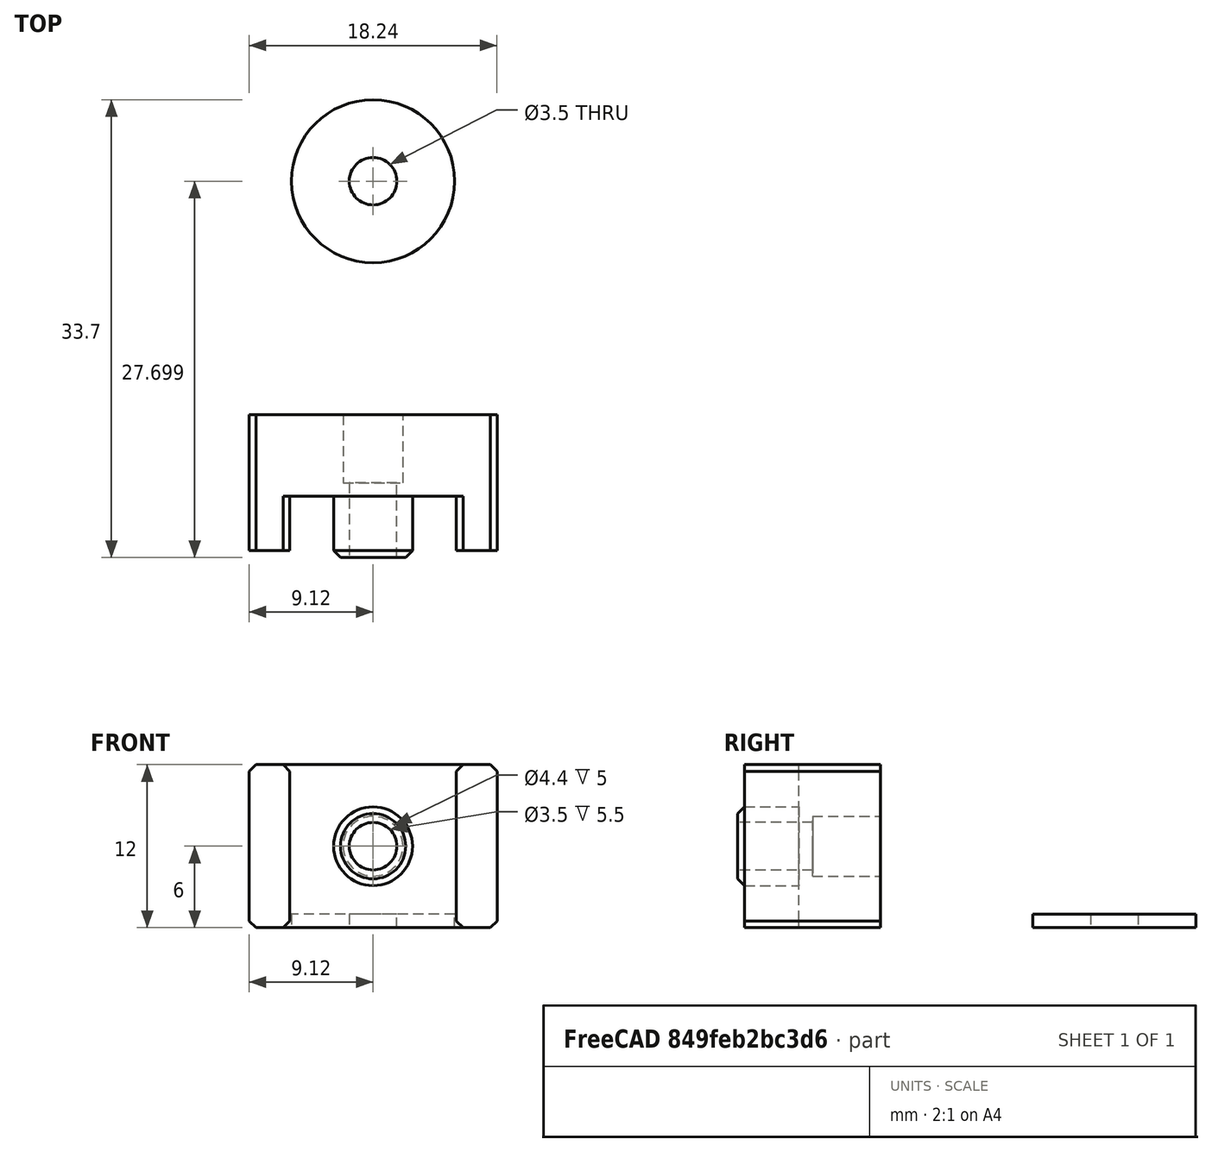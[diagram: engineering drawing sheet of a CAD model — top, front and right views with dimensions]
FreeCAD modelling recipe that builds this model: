
FCSTD DOCUMENT  (FreeCAD 0.19R)
Label: Z-rail_clips
License: All rights reserved
LicenseURL: http://en.wikipedia.org/wiki/All_rights_reserved
objects: Sketcher::SketchObject×5, PartDesign::Pad×3, PartDesign::Pocket×2, PartDesign::Chamfer×2, PartDesign::Body×2, Mesh::Feature×1
note: 21 computed .brp shape members not serialized (recipe doc carries the construction recipe); baked Part::Feature solids carry a one-line shape summary decoded from their .brp

FEATURE [Sketcher::SketchObject] Sketch
  FullyConstrained = true
  MapMode = 5
  Support = -> [XY_Plane]
  sketch-geometry (8):
    g0: LineSegment StartX=-9.125 StartY=-4 StartZ=0 EndX=-6.125 EndY=-4 EndZ=0
    g1: LineSegment StartX=-6.125 StartY=-4 StartZ=0 EndX=-6.125 EndY=0 EndZ=0
    g2: LineSegment StartX=-6.125 StartY=0 StartZ=0 EndX=6.125 EndY=0 EndZ=0
    g3: LineSegment StartX=6.125 StartY=0 StartZ=0 EndX=6.125 EndY=-4 EndZ=0
    g4: LineSegment StartX=6.125 StartY=-4 StartZ=0 EndX=9.125 EndY=-4 EndZ=0
    g5: LineSegment StartX=9.125 StartY=-4 StartZ=0 EndX=9.125 EndY=6 EndZ=0
    g6: LineSegment StartX=9.125 StartY=6 StartZ=0 EndX=-9.125 EndY=6 EndZ=0
    g7: LineSegment StartX=-9.125 StartY=6 StartZ=0 EndX=-9.125 EndY=-4 EndZ=0
  constraints (22):
    c: Horizontal(g0)
    c: Coincident(g0,g1)
    c: PointOnObject(g1,g-1)
    c: Vertical(g1)
    c: Coincident(g1,g2)
    c: PointOnObject(g2,g-1)
    c: Coincident(g2,g3)
    c: Vertical(g3)
    c: Coincident(g3,g4)
    c: Coincident(g4,g5)
    c: Vertical(g5)
    c: Coincident(g5,g6)
    c: Horizontal(g6)
    c: Coincident(g6,g7)
    c: Coincident(g7,g0)
    c: Symmetric(g0,g4,g-2)
    c: Symmetric(g3,g0,g-2)
    c: Vertical(g7)
    c: Distance(g2,g6) = 6
    c: Distance(g4) = 3
    c: Distance(g3) = 4
    c: Distance(g3,g0) = 12.25
FEATURE [PartDesign::Pad] Pad
  Direction = (1,1,1)
  Length = 12
  Length2 = 100
  Profile = -> Sketch
  Type = 0
FEATURE [Sketcher::SketchObject] Sketch001
  FullyConstrained = true
  MapMode = 5
  Placement = pos=(0,0,0) rot=(1,0,0;1.5708rad)
  Support = -> [Pad]
  sketch-geometry (1):
    g0: Circle CenterX=0 CenterY=6 CenterZ=0 NormalX=0 NormalY=0 NormalZ=1 AngleXU=0 Radius=2.9
  constraints (3):
    c: PointOnObject(g0,g-2)
    c: Diameter(g0) = 5.8
    c: DistanceY(g0) = 6
FEATURE [PartDesign::Pad] Pad001
  BaseFeature = -> Pad
  Direction = (1,1,1)
  Length = 4.5
  Length2 = 100
  Profile = -> Sketch001
  Type = 0
FEATURE [Sketcher::SketchObject] Sketch002
  FullyConstrained = true
  MapMode = 5
  Placement = pos=(0,-4.5,1e-15) rot=(1,0,0;1.5708rad)
  Support = -> [Pad001]
  sketch-geometry (1):
    g0: Circle CenterX=0 CenterY=6 CenterZ=0 NormalX=0 NormalY=0 NormalZ=1 AngleXU=0 Radius=1.75
  constraints (3):
    c: PointOnObject(g0,g-2)
    c: DistanceY(g0) = 6
    c: Diameter(g0) = 3.5
FEATURE [PartDesign::Pocket] Pocket
  BaseFeature = -> Pad001
  Length = 5
  Length2 = 100
  Profile = -> Sketch002
  Type = 1
FEATURE [Sketcher::SketchObject] Sketch003
  FullyConstrained = true
  MapMode = 5
  Placement = pos=(0,6,0) rot=(0,0.707107,0.707107;3.14159rad)
  Support = -> [Pocket]
  sketch-geometry (1):
    g0: Circle CenterX=0 CenterY=6 CenterZ=0 NormalX=0 NormalY=0 NormalZ=1 AngleXU=0 Radius=2.2
  constraints (3):
    c: PointOnObject(g0,g-2)
    c: DistanceY(g0) = 6
    c: Diameter(g0) = 4.4
FEATURE [PartDesign::Pocket] Pocket001
  BaseFeature = -> Pocket
  Length = 5
  Length2 = 100
  Profile = -> Sketch003
  Type = 0
FEATURE [PartDesign::Chamfer] Chamfer
  Angle = 45
  Base = -> Pocket001 [Edge30]
  BaseFeature = -> Pocket001
  ChamferType = 0
  FlipDirection = false
  Size = 0.5
  Size2 = 1
  SupportTransform = false
FEATURE [PartDesign::Chamfer] Chamfer001
  Angle = 45
  Base = -> Chamfer [Edge12,Edge13,Edge15,Edge17,Edge23,Edge21,Edge25,Edge19]
  BaseFeature = -> Chamfer
  ChamferType = 0
  FlipDirection = false
  Size = 0.5
  Size2 = 1
  SupportTransform = false
FEATURE [PartDesign::Body] Body
  Group = -> [Sketch,Pad,Sketch001,Pad001,Sketch002,Pocket,Sketch003,Pocket001,Chamfer,Chamfer001]
  Origin = -> Origin
  Tip = -> Chamfer001
FEATURE [Sketcher::SketchObject] Sketch004
  FullyConstrained = true
  MapMode = 5
  Support = -> [XY_Plane001]
  sketch-geometry (2):
    g0: Circle CenterX=0 CenterY=23.1994 CenterZ=0 NormalX=0 NormalY=0 NormalZ=1 AngleXU=0 Radius=6
    g1: Circle CenterX=0 CenterY=23.1994 CenterZ=0 NormalX=0 NormalY=0 NormalZ=1 AngleXU=0 Radius=1.75
  constraints (5):
    c: PointOnObject(g0,g-2)
    c: Diameter(g0) = 12
    c: Coincident(g1,g0)
    c: Block(g1)
    c: Diameter(g1) = 3.5
FEATURE [PartDesign::Pad] Pad002
  Direction = (1,1,1)
  Length = 1
  Length2 = 100
  Profile = -> Sketch004
  Type = 0
FEATURE [PartDesign::Body] Body001
  Group = -> [Sketch004,Pad002]
  Origin = -> Origin001
  Tip = -> Pad002
FEATURE [Mesh::Feature] Mesh  label="Chamfer001 (Meshed)"
